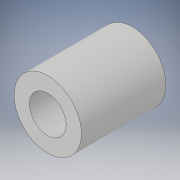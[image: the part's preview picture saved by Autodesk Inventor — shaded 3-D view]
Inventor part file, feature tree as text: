
AUTODESK INVENTOR PART (.ipt)
format: ipt  version: 2017 (Build 210142000, 142)  size: 95,744 bytes
history: native  units: in
note: dims shown in document units (in); Inventor stores cm internally (conversion verified against a paired STEP export)
features: extrude x1, sketch x1
ambient origin geometry x8: Origin, YZ Plane, XZ Plane, XY Plane, X Axis, Y Axis, Z Axis, Center Point
bodies: Solid1 (feature_tree)
feature tree (2):
  extrude  "Extrusion1"  Depth=0.69in
  sketch  "Sketch1"  dims[d0=0.3in d1=0.55in d2=0.69in d3=0.0in]
